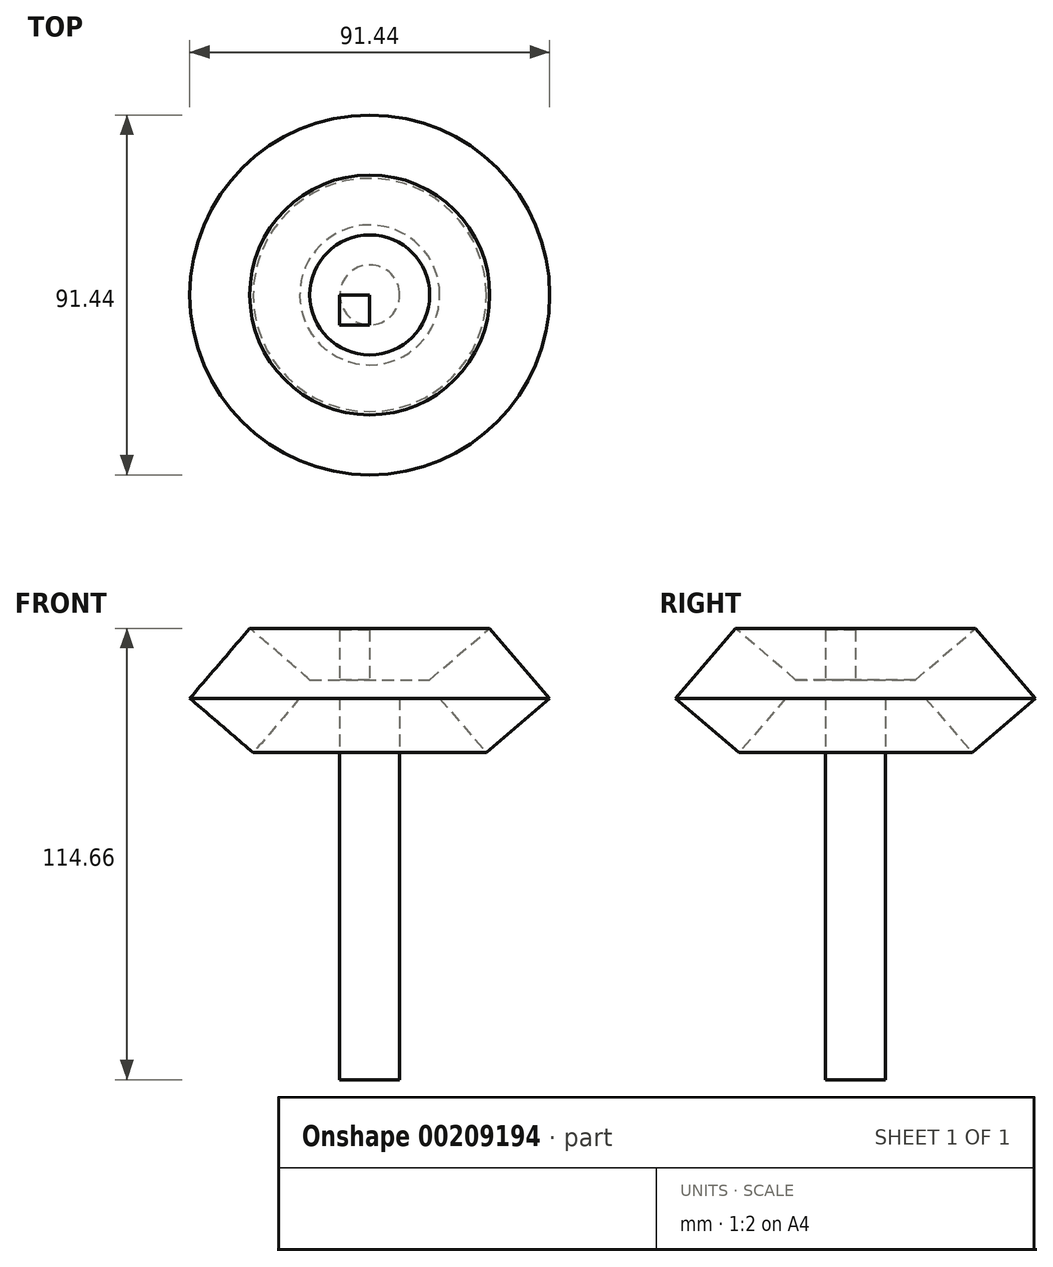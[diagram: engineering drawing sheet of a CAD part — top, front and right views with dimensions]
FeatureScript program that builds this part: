
annotation { "Feature Type Name" : "Feature", "Feature Type Description" : "" }
export const myFeature = defineFeature(function(context is Context, id is Id, definition is map)
    precondition{}
    {
        {
            var Q0;
            Q0=qCreatedBy(makeId("Front.planeOp"),FACE);
            var sketch = newSketch(context, id + "F0", { "sketchPlane" : qUnion([Q0])});
            skLineSegment(sketch, "E0", {"start": v(0, 20.32) * mm, "end": v(15.24, 20.32) * mm});
            skLineSegment(sketch, "E1", {"start": v(15.24, 20.32) * mm, "end": v(30.48, 33.38) * mm});
            skLineSegment(sketch, "E2", {"start": v(30.48, 33.38) * mm, "end": v(45.72, 15.6) * mm});
            skLineSegment(sketch, "E3", {"start": v(45.72, 15.6) * mm, "end": v(29.61, 1.8) * mm});
            skLineSegment(sketch, "E4", {"start": v(29.61, 1.8) * mm, "end": v(17.78, 15.6) * mm});
            skLineSegment(sketch, "E5", {"start": v(17.78, 15.6) * mm, "end": v(7.62, 15.6) * mm});
            skLineSegment(sketch, "E6", {"start": v(7.62, 15.6) * mm, "end": v(7.62, -81.28) * mm});
            skLineSegment(sketch, "E7", {"start": v(7.62, -81.28) * mm, "end": v(0, -81.28) * mm});
            skLineSegment(sketch, "E8", {"start": v(0, -81.28) * mm, "end": v(0, 20.32) * mm});
            skSolve(sketch);
        }
        {
            var Q0;
            Q0 = qSketchRegion(id + "F0", true);
            var Q1;
            Q1=sQuery(id+"F0.wireOp",EDGE,"E8");
            revolve(context, id + "F1", {"entities" : qUnion([Q0]), "axis" : qUnion([Q1]), "revolveType" : RevolveType.FULL});
        }
        {
            var Q0;
            Q0=makeQuery(id+"F1.opRevolve","SWEPT_FACE",FACE,{"disambiguationData":[OSD([sQuery(id+"F0.wireOp",EDGE,"E0")])]});
            var sketch = newSketch(context, id + "F2", { "sketchPlane" : qUnion([Q0])});
            skLineSegment(sketch, "E9.bottom", {"start": v(0, 0) * mm, "end": v(-7.62, 0) * mm});
            skLineSegment(sketch, "E9.top", {"start": v(0, -7.62) * mm, "end": v(-7.62, -7.62) * mm});
            skLineSegment(sketch, "E9.left", {"start": v(0, 0) * mm, "end": v(0, -7.62) * mm});
            skLineSegment(sketch, "E9.right", {"start": v(-7.62, 0) * mm, "end": v(-7.62, -7.62) * mm});
            skSolve(sketch);
        }
        {
            var Q0;
            Q0 = qSketchRegion(id + "F2", true);
            extrude(context, id + "F3", {"entities" : qUnion([Q0]), "operationType" : NewBodyOperationType.ADD, "depth" : 12.7 * mm});
        }
    });
